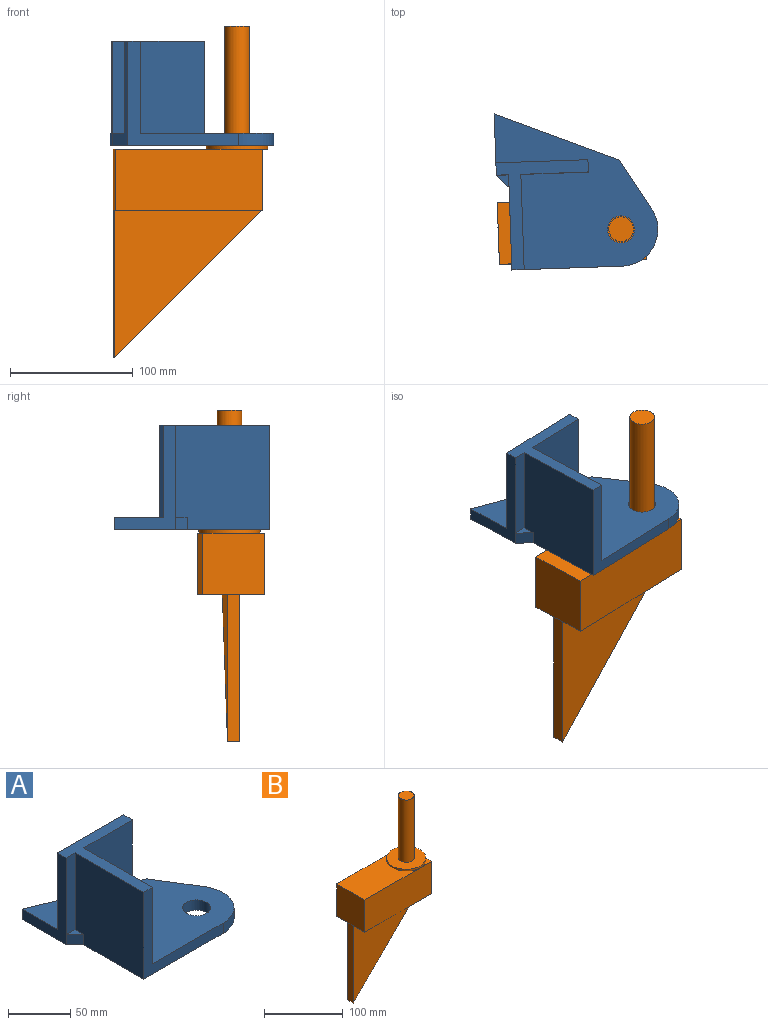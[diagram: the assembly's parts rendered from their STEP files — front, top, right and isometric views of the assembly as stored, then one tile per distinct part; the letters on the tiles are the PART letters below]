
ASSEMBLY  parts=2 mates=1
PART A: 17 faces, bbox 130x127.5x85 mm
  f0: plane 10x10mm, normal (0,0,1), area 50mm2, adj f2,f3,f11
  f1: plane 130x127.5mm, normal (0,0,1), area 9715.9mm2, adj f4,f5,f6,f7,f8,f9,f13,f14
  f2: plane 85x77.5mm, normal (-1,0,0), area 6487.5mm2, adj f0,f3,f9,f10,f11,f12
  f3: plane 10x10mm, normal (-0.71,-0.71,0), area 141.4mm2, adj f0,f2,f4,f10
  f4: plane 85x50mm, normal (-1,0,0), area 1250mm2, adj f1,f3,f5,f10,f11,f12,f14
  f5: plane 100.26x40.86mm, normal (0.38,0.93,0), area 1082.7mm2, adj f1,f4,f6,f10
  f6: plane 40.86x25.26mm, normal (0.85,0.53,0), area 480.4mm2, adj f1,f5,f7,f10
  f7: cylinder r=30mm len=45.77mm, axis (0,0,-1), area 637.3mm2, adj f1,f6,f9,f10
  f8: cylinder r=11mm len=22mm, axis (0,0,-1), area 691.2mm2, adj f1,f10
  f9: plane 90x85mm, normal (0,-1,0), area 1650mm2, adj f1,f2,f7,f10,f12,f16
  f10: plane 130x127.5mm, normal (0,0,-1), area 11290.9mm2, adj f2,f3,f4,f5,f6,f7,f8,f9
  f11: plane 75x10mm, normal (0,-1,0), area 750mm2, adj f0,f2,f4,f12
  f12: plane 87.5x75mm, normal (0,0,1), area 1525mm2, adj f2,f4,f9,f11,f13,f14,f15,f16
  f13: plane 75x10mm, normal (1,0,0), area 750mm2, adj f1,f12,f14,f15
  f14: plane 75x75mm, normal (0,1,0), area 5625mm2, adj f1,f4,f12,f13
  f15: plane 75x55mm, normal (0,-1,0), area 4125mm2, adj f1,f12,f13,f16
  f16: plane 77.5x75mm, normal (1,0,0), area 5812.5mm2, adj f1,f9,f12,f15
PART B: 18 faces, bbox 125.1x50x270 mm
  f0: plane 20x10mm, normal (0,0,1), area 60.2mm2, adj f6,f7,f14
  f1: plane 100x50mm, normal (0,0,1), area 4018.3mm2, adj f4,f5,f7,f14
  f2: plane 20x10mm, normal (0,0,1), area 60.2mm2, adj f5,f6,f14
  f3: plane 120x50mm, normal (0,0,-1), area 4801.2mm2, adj f4,f5,f6,f7,f10,f11,f12
  f4: plane 50x50mm, normal (-1,0,0), area 2500mm2, adj f1,f3,f5,f7,f8
  f5: plane 120x50mm, normal (0,-1,0), area 6000mm2, adj f1,f2,f3,f4,f6
  f6: plane 50x50mm, normal (1,0,0), area 2500mm2, adj f0,f2,f3,f5,f7,f13
  f7: plane 120x50mm, normal (0,1,0), area 6000mm2, adj f0,f1,f3,f4,f6
  f8: plane 10x0.12mm, normal (0,0,1), area 1.2mm2, adj f4,f9,f11,f12
  f9: plane 120x10mm, normal (-1,0,0), area 1200mm2, adj f8,f10,f11,f12
  f10: plane 120x120mm, normal (0.71,0,-0.71), area 1697.1mm2, adj f3,f9,f11,f12
  f11: plane 120x120mm, normal (0,-1,0), area 7200mm2, adj f3,f8,f9,f10
  f12: plane 120x120mm, normal (0,1,0), area 7200mm2, adj f3,f8,f9,f10
  f13: plane 30x5mm, normal (0,0,-1), area 102.2mm2, adj f6,f14
  f14: cylinder r=25mm len=50mm, axis (0,0,-1), area 471.2mm2, adj f0,f1,f2,f13,f15
  f15: plane 50x50mm, normal (0,0,1), area 1649.3mm2, adj f14,f17
  f16: plane 20x20mm, normal (0,0,1), area 314.2mm2, adj f17
  f17: cylinder r=10mm len=97mm, axis (0,0,-1), area 6094.7mm2, adj f15,f16
PLACE A rot(axis=(0,0,1),2deg) t=(1.37,-3.47,0)mm
PLACE B rot(axis=(0,0,1),2deg) t=(60.02,36.1,-53)mm
MATE revolute B.f14 <-> A.f7  axis (0,0,1) through (100,37.5,0)mm
